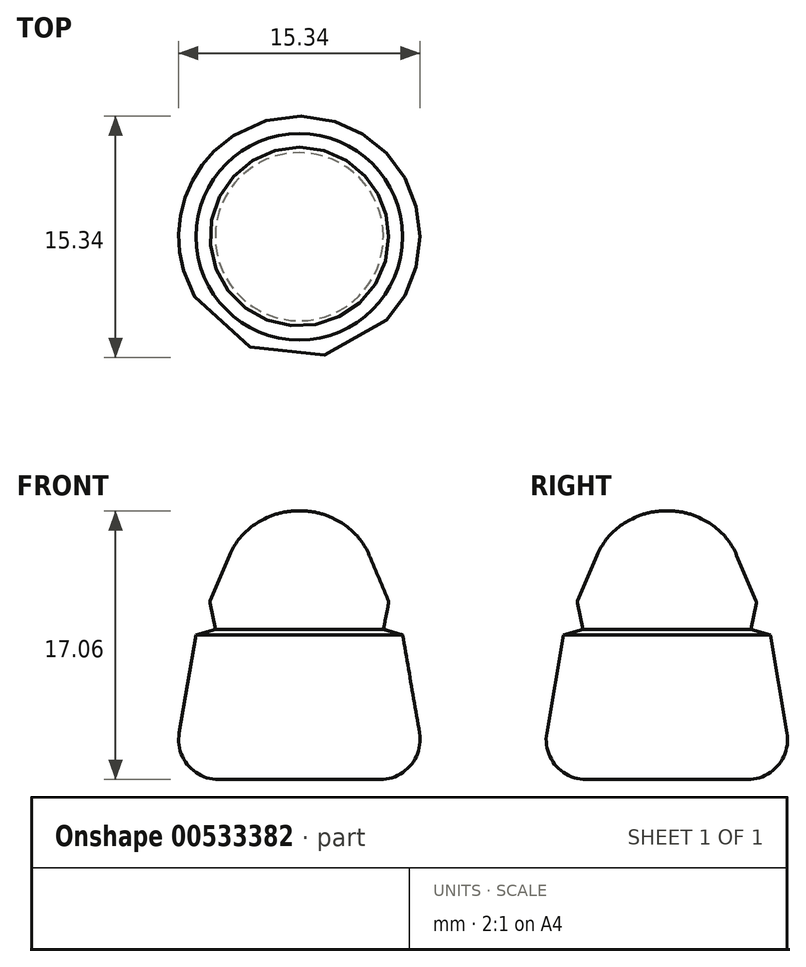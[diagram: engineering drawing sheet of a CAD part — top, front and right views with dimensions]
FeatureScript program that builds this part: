
annotation { "Feature Type Name" : "Feature", "Feature Type Description" : "" }
export const myFeature = defineFeature(function(context is Context, id is Id, definition is map)
    precondition{}
    {
        {
            var Q0;
            Q0=qCreatedBy(makeId("Front.planeOp"),FACE);
            var sketch = newSketch(context, id + "F0", { "sketchPlane" : qUnion([Q0])});
            skLineSegment(sketch, "E0", {"start": v(0, 0) * mm, "end": v(-8.14, 0) * mm});
            skLineSegment(sketch, "E1", {"start": v(-8.14, 0) * mm, "end": v(-6.56, 9.19) * mm});
            skLineSegment(sketch, "E2", {"start": v(-6.56, 9.19) * mm, "end": v(-5.34, 9.54) * mm});
            skLineSegment(sketch, "E3", {"start": v(-5.34, 9.54) * mm, "end": v(-5.69, 11.29) * mm});
            skLineSegment(sketch, "E4", {"start": v(-5.69, 11.29) * mm, "end": v(-3.76, 15.84) * mm});
            skLineSegment(sketch, "E5", {"start": v(-3.76, 15.84) * mm, "end": v(-1.14, 17.06) * mm});
            skLineSegment(sketch, "E6", {"start": v(-1.14, 17.06) * mm, "end": v(0, 17.06) * mm});
            skLineSegment(sketch, "E7", {"start": v(0, 17.06) * mm, "end": v(0, 0) * mm});
            skSolve(sketch);
        }
        {
            var Q0;
            Q0=makeQuery(id+"F0.imprint","IMPRINT",FACE,{"disambiguationData":[TD([[makeQuery(id+"F0.imprint","IMPRINT",EDGE,{"derivedFrom":sQuery(id+"F0.wireOp",EDGE,"E0")}),-1.0]])]});
            var Q1;
            Q1=sQuery(id+"F0.wireOp",EDGE,"E7");
            revolve(context, id + "F1", {"entities" : qUnion([Q0]), "axis" : qUnion([Q1]), "revolveType" : RevolveType.FULL});
        }
        {
            var Q0;
            Q0=makeQuery(id+"F1.opRevolve","SWEPT_FACE",FACE,{"disambiguationData":[OSD([sQuery(id+"F0.wireOp",EDGE,"E5")])]});
            fillet(context, id + "F2", {"entities" : qUnion([Q0]), "radius" : 4.5 * mm, "tangentPropagation" : true, "allowEdgeOverflow" : false});
        }
        {
            var Q0;
            Q0=makeQuery(id+"F1.opRevolve","SWEPT_FACE",FACE,{"disambiguationData":[OSD([sQuery(id+"F0.wireOp",EDGE,"E4")])]});
            fillet(context, id + "F3", {"entities" : qUnion([Q0]), "radius" : 0.22 * mm, "tangentPropagation" : true, "allowEdgeOverflow" : false});
        }
        {
            var Q0;
            Q0=makeQuery(id+"F1.opRevolve","SWEPT_EDGE",EDGE,{"disambiguationData":[OSD([sQuery(id+"F0.wireOp",EDGE,"E0"),sQuery(id+"F0.wireOp",EDGE,"E1")])]});
            fillet(context, id + "F4", {"entities" : qUnion([Q0]), "radius" : 2.54 * mm, "tangentPropagation" : true, "allowEdgeOverflow" : false});
        }
    });
